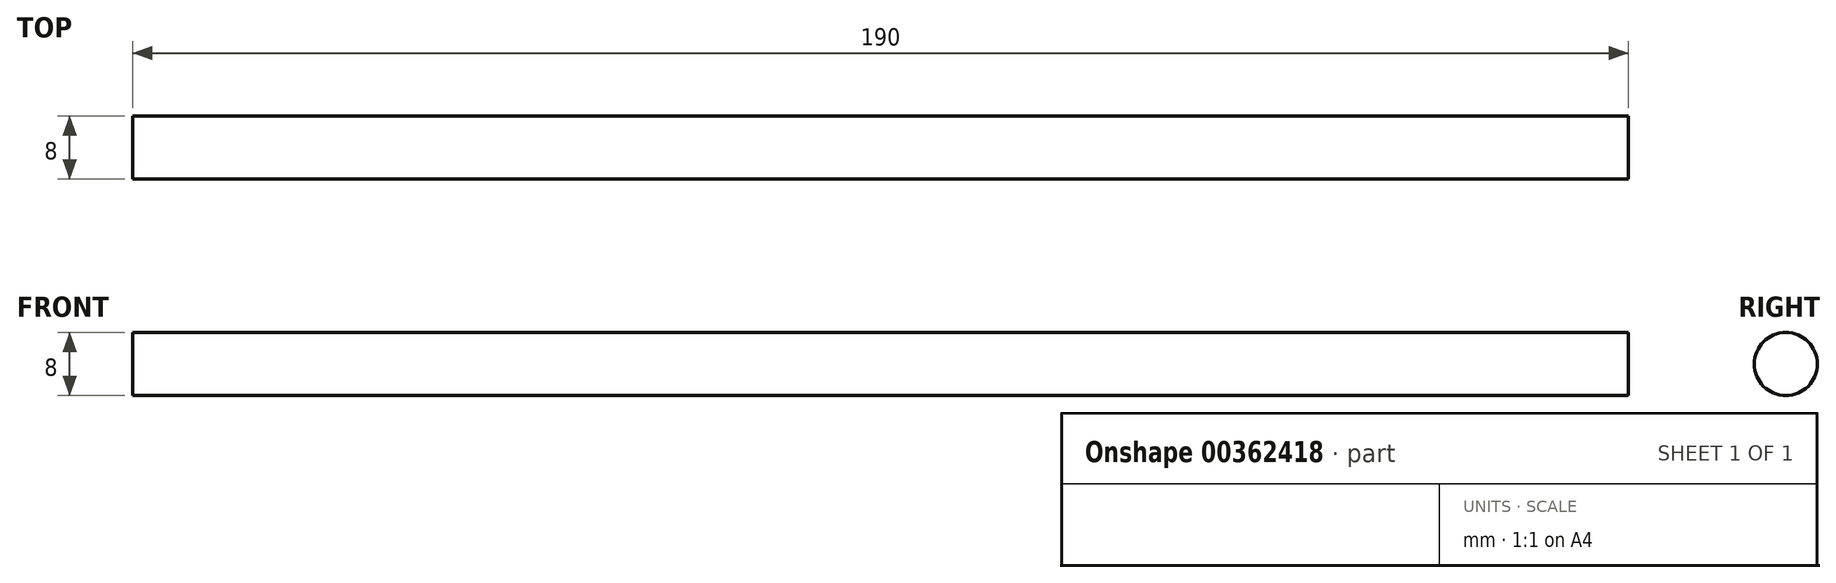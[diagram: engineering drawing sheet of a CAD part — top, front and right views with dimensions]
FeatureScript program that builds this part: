
annotation { "Feature Type Name" : "Feature", "Feature Type Description" : "" }
export const myFeature = defineFeature(function(context is Context, id is Id, definition is map)
    precondition{}
    {
        {
            var Q0;
            Q0=qCreatedBy(makeId("Right.planeOp"),FACE);
            var sketch = newSketch(context, id + "F0", { "sketchPlane" : qUnion([Q0])});
            skCircle(sketch, "E0", {"center": v(0, 0) * mm, "radius": 4 * mm});
            skSolve(sketch);
        }
        {
            var Q0;
            Q0=qSketchRegion(id+"F0",true);
            extrude(context, id + "F1", {"entities" : qUnion([Q0]), "endBound" : BoundingType.SYMMETRIC, "depth" : 190 * mm});
        }
    });
